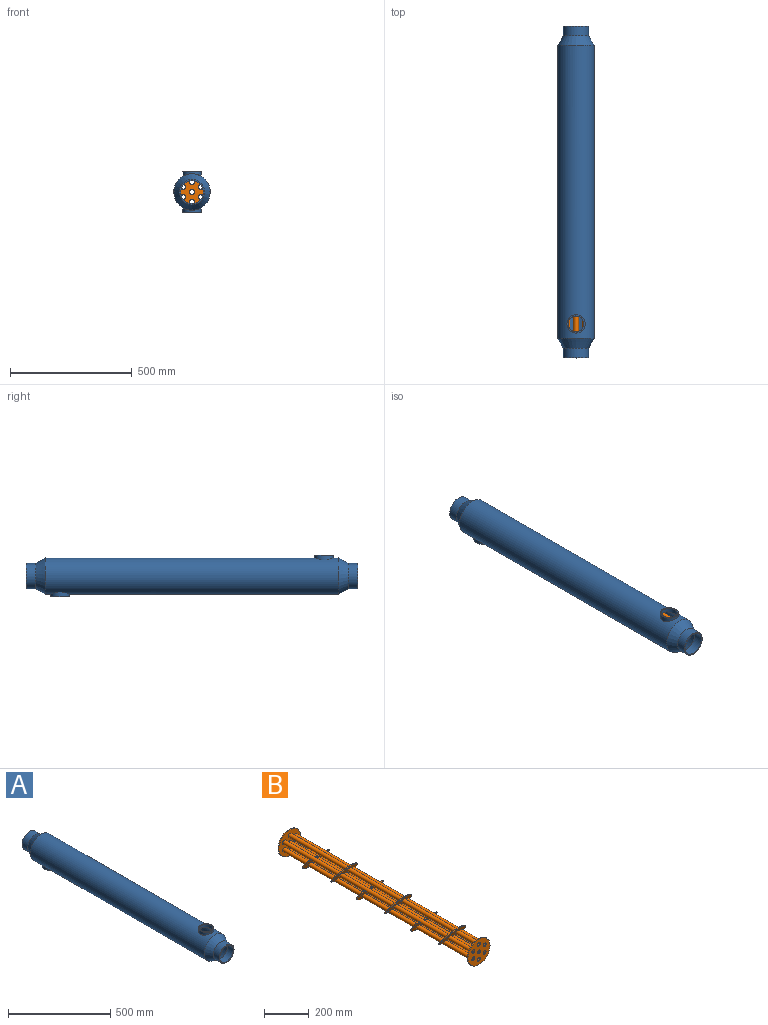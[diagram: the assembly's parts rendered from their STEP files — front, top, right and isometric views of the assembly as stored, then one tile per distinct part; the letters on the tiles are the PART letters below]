
ASSEMBLY  parts=2 mates=2
PART A: 18 faces, bbox 150x1365x170 mm
  f0: cylinder r=75mm len=1205mm, axis (0,-1,0), area 558717mm2, adj f2,f3,f14,f17
  f1: cylinder r=70mm len=1205mm, axis (0,-1,0), area 523166.6mm2, adj f7,f8,f12,f15
  f2: cone r=51.8mm half-angle=30.1deg, axis (0,-1,0), area 18420.3mm2, adj f0,f11
  f3: cone r=51.8mm half-angle=30.1deg, axis (0,1,0), area 18420.3mm2, adj f0,f4
  f4: cylinder r=51.8mm len=103.6mm, axis (0,-1,0), area 13018.8mm2, adj f3,f5
  f5: plane 103.6x103.6mm, normal (0,-1,0), area 1548.8mm2, adj f4,f6
  f6: cylinder r=46.8mm len=93.6mm, axis (0,-1,0), area 11762.2mm2, adj f5,f7
  f7: cone r=70mm half-angle=30.1deg, axis (0,1,0), area 16967.6mm2, adj f1,f6
  f8: cone r=70mm half-angle=30.1deg, axis (0,-1,0), area 16967.6mm2, adj f1,f9
  f9: cylinder r=46.8mm len=93.6mm, axis (0,-1,0), area 11762.2mm2, adj f8,f10
  f10: plane 103.6x103.6mm, normal (0,1,0), area 1548.8mm2, adj f9,f11
  f11: cylinder r=51.8mm len=103.6mm, axis (0,-1,0), area 13018.8mm2, adj f2,f10
  f12: cylinder r=32.5mm len=65mm, axis (0,0,1), area 3866.5mm2, adj f1,f16
  f13: plane 75x75mm, normal (0,0,-1), area 1099.6mm2, adj f14,f15
  f14: cylinder r=37.5mm len=75mm, axis (0,0,-1), area 3518.8mm2, adj f0,f13
  f15: cylinder r=32.5mm len=65mm, axis (0,0,-1), area 3867.9mm2, adj f1,f13
  f16: plane 75x75mm, normal (0,0,1), area 1099.6mm2, adj f12,f17
  f17: cylinder r=37.5mm len=75mm, axis (0,0,1), area 3518.1mm2, adj f0,f16
PART B: 80 faces, bbox 143.2x1208.2x143.2 mm
  f0: plane 140x140mm, normal (0,1,0), area 13409.1mm2, adj f1,f3,f4,f5,f6,f7,f8,f9
  f1: cylinder r=70mm len=140mm, axis (0,1,0), area 2199.1mm2, adj f0,f2
  f2: plane 140x140mm, normal (0,-1,0), area 12969.3mm2, adj f1,f10,f26,f27,f73,f74,f75,f76
  f3: cylinder r=9.5mm len=1205mm, axis (0,-1,0), area 71926.8mm2, adj f0,f11
  f4: cylinder r=9.5mm len=1205mm, axis (0,-1,0), area 71926.8mm2, adj f0,f11
  f5: cylinder r=9.5mm len=1205mm, axis (0,-1,0), area 71926.8mm2, adj f0,f11
  f6: cylinder r=9.5mm len=1205mm, axis (0,-1,0), area 71926.8mm2, adj f0,f11
  f7: cylinder r=9.5mm len=1205mm, axis (0,-1,0), area 71926.8mm2, adj f0,f11
  f8: cylinder r=9.5mm len=1205mm, axis (0,-1,0), area 71926.8mm2, adj f0,f11
  f9: cylinder r=9.5mm len=1205mm, axis (0,-1,0), area 71926.8mm2, adj f0,f11
  f10: cylinder r=10.5mm len=144.52mm, axis (0,-1,0), area 9049.5mm2, adj f2,f22
  f11: plane 140x140mm, normal (0,-1,0), area 13409.1mm2, adj f3,f4,f5,f6,f7,f8,f9,f13
  f12: plane 140x140mm, normal (0,1,0), area 12969.3mm2, adj f13,f14,f15,f16,f17,f18,f19,f77
  f13: cylinder r=70mm len=140mm, axis (0,1,0), area 2199.1mm2, adj f11,f12
  f14: cylinder r=10.5mm len=359mm, axis (0,-1,0), area 22992.3mm2, adj f12,f44,f50,f52,f53,f54
  f15: cylinder r=10.5mm len=158.87mm, axis (0,-1,0), area 9995.9mm2, adj f12,f50
  f16: cylinder r=10.5mm len=144.51mm, axis (0,-1,0), area 9048.9mm2, adj f12,f50
  f17: cylinder r=10.5mm len=173.22mm, axis (0,-1,0), area 10942.9mm2, adj f12,f50
  f18: cylinder r=10.5mm len=158.87mm, axis (0,-1,0), area 9995.9mm2, adj f12,f50
  f19: cylinder r=10.5mm len=359mm, axis (0,-1,0), area 22992.3mm2, adj f12,f44,f49,f50,f52,f54
  f20: plane 20.78x6.1mm, normal (0,0,1), area 126.8mm2, adj f22,f23,f24,f73
  f21: plane 50.04x6.1mm, normal (0,0,1), area 305.4mm2, adj f22,f24,f26,f73
  f22: plane 143.2x94.2mm, normal (0,0.82,0.57), area 10790.9mm2, adj f10,f20,f21,f23,f25,f26,f73,f74
  f23: cylinder r=70mm len=140mm, axis (0,1,0), area 1602.7mm2, adj f20,f22,f24,f25
  f24: plane 143.2x94.2mm, normal (0,-0.82,-0.57), area 10790.9mm2, adj f20,f21,f23,f25,f26,f28,f29,f66
  f25: plane 20.78x6.1mm, normal (0,0,1), area 126.8mm2, adj f22,f23,f24,f26
  f26: cylinder r=10.5mm len=359.01mm, axis (0,-1,0), area 22992.9mm2, adj f2,f21,f22,f24,f25,f70
  f27: cylinder r=10.5mm len=373.37mm, axis (0,-1,0), area 24147.4mm2, adj f2,f70
  f28: cylinder r=10.5mm len=180.14mm, axis (0,-1,0), area 10907.1mm2, adj f24,f70
  f29: cylinder r=10.5mm len=351.57mm, axis (0,-1,0), area 22009.5mm2, adj f24,f32,f68,f70,f71,f72
  f30: plane 20.78x6.1mm, normal (0,0,1), area 126.8mm2, adj f32,f33,f34,f64
  f31: plane 50.04x6.1mm, normal (0,0,1), area 305.4mm2, adj f32,f34,f36,f64
  f32: plane 140x91mm, normal (0,0.82,0.57), area 10790.9mm2, adj f29,f30,f31,f33,f35,f36,f64,f65
  f33: cylinder r=70mm len=140mm, axis (0,1,0), area 1602.7mm2, adj f30,f32,f34,f35
  f34: plane 140x91mm, normal (0,-0.82,-0.57), area 10790.9mm2, adj f30,f31,f33,f35,f36,f38,f39,f57
  f35: plane 20.78x6.1mm, normal (0,0,1), area 126.8mm2, adj f32,f33,f34,f36
  f36: cylinder r=10.5mm len=351.57mm, axis (0,-1,0), area 22009.5mm2, adj f31,f32,f34,f35,f61,f68
  f37: cylinder r=10.5mm len=351.57mm, axis (0,-1,0), area 22217mm2, adj f61,f68
  f38: cylinder r=10.5mm len=180.14mm, axis (0,-1,0), area 10907.1mm2, adj f34,f61
  f39: cylinder r=10.5mm len=351.57mm, axis (0,-1,0), area 22009.5mm2, adj f34,f42,f59,f61,f62,f63
  f40: plane 20.78x6.1mm, normal (0,0,1), area 126.8mm2, adj f42,f43,f44,f55
  f41: plane 50.04x6.1mm, normal (0,0,1), area 305.4mm2, adj f42,f44,f46,f55
  f42: plane 140x91mm, normal (0,0.82,0.57), area 10790.9mm2, adj f39,f40,f41,f43,f45,f46,f55,f56
  f43: cylinder r=70mm len=140mm, axis (0,1,0), area 1602.7mm2, adj f40,f42,f44,f45
  f44: plane 143.09x94.09mm, normal (0,-0.82,-0.57), area 10790.9mm2, adj f14,f19,f40,f41,f43,f45,f46,f48
  f45: plane 20.78x6.1mm, normal (0,0,1), area 126.8mm2, adj f42,f43,f44,f46
  f46: cylinder r=10.5mm len=351.57mm, axis (0,-1,0), area 22009.5mm2, adj f41,f42,f44,f45,f52,f59
  f47: cylinder r=10.5mm len=351.57mm, axis (0,-1,0), area 22217mm2, adj f52,f59
  f48: cylinder r=10.5mm len=180.14mm, axis (0,-1,0), area 10907.1mm2, adj f44,f52
  f49: plane 20.78x6.1mm, normal (0,0,-1), area 126.8mm2, adj f19,f50,f51,f52
  f50: plane 143.09x94.09mm, normal (0,-0.82,-0.57), area 10790.9mm2, adj f14,f15,f16,f17,f18,f19,f49,f51
  f51: cylinder r=70mm len=140mm, axis (0,1,0), area 1602.7mm2, adj f49,f50,f52,f53
  f52: plane 140x91mm, normal (0,0.82,0.57), area 10790.9mm2, adj f14,f19,f46,f47,f48,f49,f51,f53
  f53: plane 20.78x6.1mm, normal (0,0,-1), area 126.8mm2, adj f14,f50,f51,f52
  f54: plane 50.04x6.1mm, normal (0,0,-1), area 305.4mm2, adj f14,f19,f50,f52
  f55: cylinder r=10.5mm len=351.57mm, axis (0,-1,0), area 22009.5mm2, adj f40,f41,f42,f44,f52,f59
  f56: cylinder r=10.5mm len=180.14mm, axis (0,-1,0), area 10907.1mm2, adj f42,f59
  f57: cylinder r=10.5mm len=351.57mm, axis (0,-1,0), area 22009.5mm2, adj f34,f42,f58,f59,f61,f63
  f58: plane 20.78x6.1mm, normal (0,0,-1), area 126.8mm2, adj f57,f59,f60,f61
  f59: plane 143.2x94.2mm, normal (0,-0.82,-0.57), area 10790.9mm2, adj f39,f46,f47,f55,f56,f57,f58,f60
  f60: cylinder r=70mm len=140mm, axis (0,1,0), area 1602.7mm2, adj f58,f59,f61,f62
  f61: plane 143.2x94.2mm, normal (0,0.82,0.57), area 10790.9mm2, adj f36,f37,f38,f39,f57,f58,f60,f62
  f62: plane 20.78x6.1mm, normal (0,0,-1), area 126.8mm2, adj f39,f59,f60,f61
  f63: plane 50.04x6.1mm, normal (0,0,-1), area 305.4mm2, adj f39,f57,f59,f61
  f64: cylinder r=10.5mm len=351.57mm, axis (0,-1,0), area 22009.5mm2, adj f30,f31,f32,f34,f61,f68
  f65: cylinder r=10.5mm len=180.14mm, axis (0,-1,0), area 10907.1mm2, adj f32,f68
  f66: cylinder r=10.5mm len=351.57mm, axis (0,-1,0), area 22009.5mm2, adj f24,f32,f67,f68,f70,f72
  f67: plane 20.78x6.1mm, normal (0,0,-1), area 126.8mm2, adj f66,f68,f69,f70
  f68: plane 143.2x94.2mm, normal (0,-0.82,-0.57), area 10790.9mm2, adj f29,f36,f37,f64,f65,f66,f67,f69
  f69: cylinder r=70mm len=140mm, axis (0,1,0), area 1602.7mm2, adj f67,f68,f70,f71
  f70: plane 143.2x94.2mm, normal (0,0.82,0.57), area 10790.9mm2, adj f26,f27,f28,f29,f66,f67,f69,f71
  f71: plane 20.78x6.1mm, normal (0,0,-1), area 126.8mm2, adj f29,f68,f69,f70
  f72: plane 50.04x6.1mm, normal (0,0,-1), area 305.4mm2, adj f29,f66,f68,f70
  f73: cylinder r=10.5mm len=359.01mm, axis (0,-1,0), area 22992.9mm2, adj f2,f20,f21,f22,f24,f70
  f74: cylinder r=10.5mm len=173.23mm, axis (0,-1,0), area 10943.5mm2, adj f2,f22
  f75: cylinder r=10.5mm len=158.88mm, axis (0,-1,0), area 9996.5mm2, adj f2,f22
  f76: cylinder r=10.5mm len=158.88mm, axis (0,-1,0), area 9996.5mm2, adj f2,f22
  f77: cylinder r=10.5mm len=373.36mm, axis (0,-1,0), area 24146.7mm2, adj f12,f44
  f78: cylinder r=10.5mm len=351.57mm, axis (0,-1,0), area 22217mm2, adj f34,f42
  f79: cylinder r=10.5mm len=351.57mm, axis (0,-1,0), area 22217mm2, adj f24,f32
PLACE A t=(-401.32,-562.04,-305.85)mm
PLACE B t=(-401.32,37.96,-305.85)mm
MATE cylindrical A.f0 <-> B.f1  axis (0,-1,0) through (-401.32,-562.04,-305.85)mm
MATE fastened A.f0 <-> B.f1  axis (0,-1,0) through (-401.32,-1164.54,-305.85)mm
